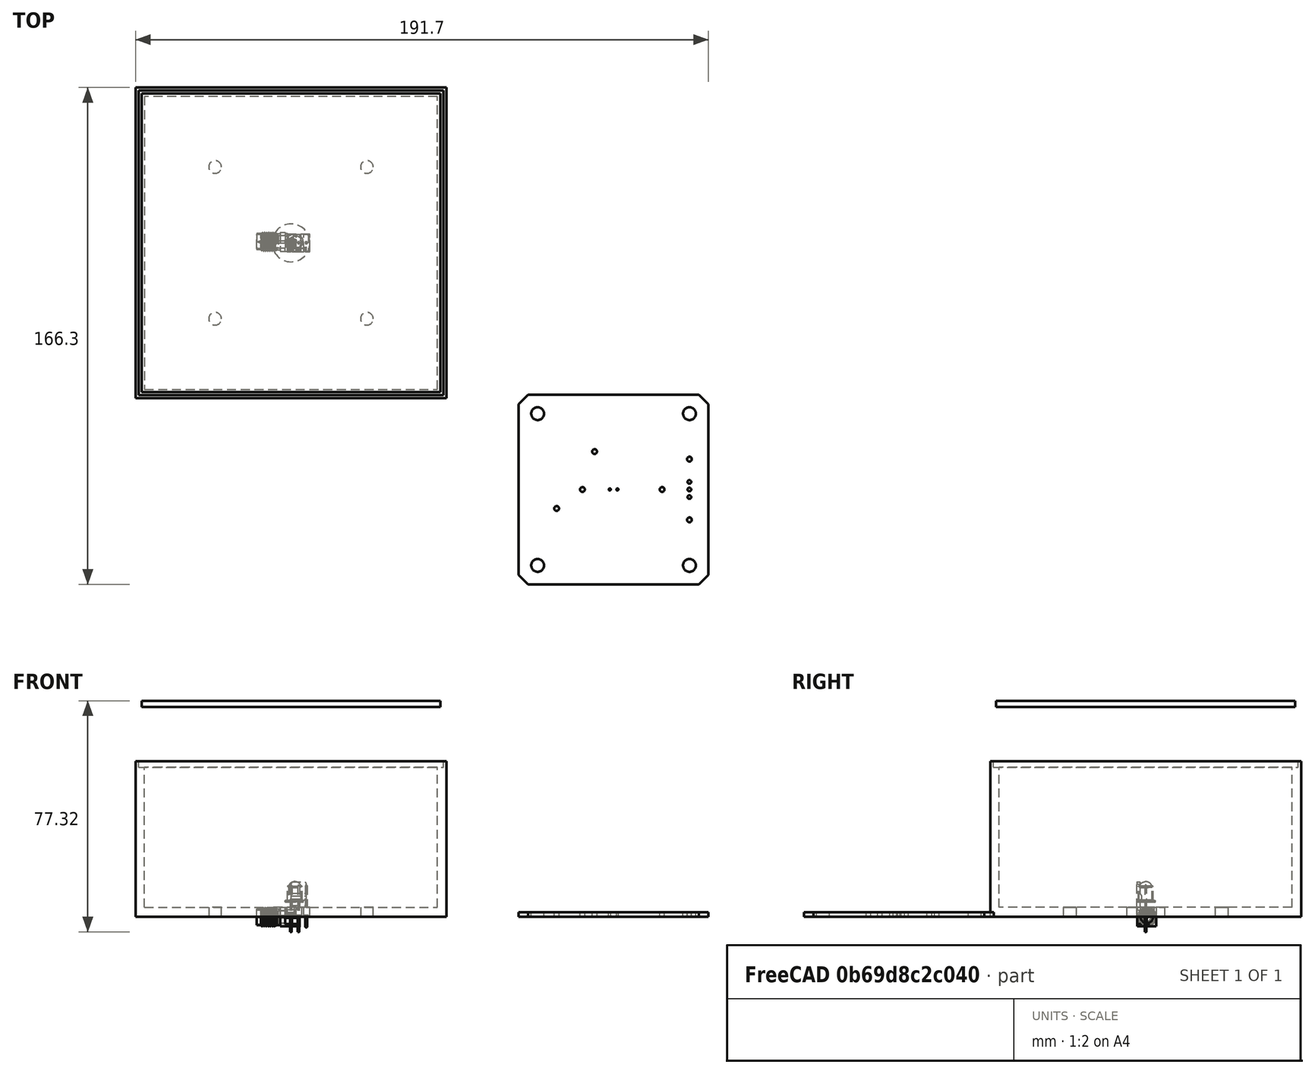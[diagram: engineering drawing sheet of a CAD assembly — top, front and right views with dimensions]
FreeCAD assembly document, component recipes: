
FREECAD ASSEMBLY — COMPONENT RECIPES ("Lensmount")

This assembly document has 3 components, labeled P0..P2 below (a component is one placed body or linked part). 2 of them carry a construction recipe — the FreeCAD feature program that regenerates the part from scratch, quoted from this document or its linked companion documents; the rest are supplied as boundary geometry only. No exploded tour is included for this assembly.
COMPONENT P0 — geometry summary ("ADA4610 Transimpedance Amplifier 1"; no construction recipe available for this part):
  bounding box: 73.0 x 63.5 x 18.9 mm
  tessellated surface: 3,265 triangles
  volume: 51078090254027713934101195006140775365494435911598212671501187176010288595226610358736377589302034432 mm^3 (58298447673324615155903128428619562438456596439960692855769413962441940173557407954676489648078848% of its bounding box)
COMPONENT P1 — recipe-attached ("PCB Mount", modeled in this document).
Construction recipe (the document's own serialized feature program — sketch geometry with constraints, then the solid features built on it; lengths are millimeters unless a unit is written):

FEATURE [Sketcher::SketchObject] Sketch
  FullyConstrained = true
  MapMode = 5
  Support = -> [XY_Plane024]
  sketch-geometry (11):
    g0: LineSegment StartX=-52 StartY=-52 StartZ=0 EndX=52 EndY=-52 EndZ=0
    g1: LineSegment StartX=52 StartY=-52 StartZ=0 EndX=52 EndY=52 EndZ=0
    g2: LineSegment StartX=52 StartY=52 StartZ=0 EndX=-52 EndY=52 EndZ=0
    g3: LineSegment StartX=-52 StartY=52 StartZ=0 EndX=-52 EndY=-52 EndZ=0
    g4: LineSegment StartX=-52 StartY=-52 StartZ=0 EndX=52 EndY=52 EndZ=0
    g5: LineSegment StartX=-52 StartY=52 StartZ=0 EndX=52 EndY=-52 EndZ=0
    g6: Circle CenterX=-25.4 CenterY=25.4 CenterZ=0 NormalX=0 NormalY=0 NormalZ=1 AngleXU=0 Radius=2.125
    g7: Circle CenterX=25.4 CenterY=25.4 CenterZ=0 NormalX=0 NormalY=0 NormalZ=1 AngleXU=0 Radius=2.125
    g8: Circle CenterX=25.4 CenterY=-25.4 CenterZ=0 NormalX=0 NormalY=0 NormalZ=1 AngleXU=0 Radius=2.125
    g9: Circle CenterX=-25.4 CenterY=-25.4 CenterZ=0 NormalX=0 NormalY=0 NormalZ=1 AngleXU=0 Radius=2.125
    g10: Circle CenterX=0 CenterY=0 CenterZ=0 NormalX=0 NormalY=0 NormalZ=1 AngleXU=0 Radius=6.35
  constraints (30):
    c: Horizontal(g0)
    c: Horizontal(g2)
    c: Vertical(g1)
    c: Vertical(g3)
    c: DistanceX(g4,g5) = 104
    c: DistanceY(g4,g5) = 104
    c: PointOnObject(g-1,g5)
    c: PointOnObject(g-1,g4)
    c: PointOnObject(g6,g5)
    c: PointOnObject(g7,g4)
    c: PointOnObject(g8,g5)
    c: PointOnObject(g9,g4)
    c: Equal(g6,g7)
    c: Equal(g6,g8)
    c: Equal(g6,g9)
    c: Radius(g6) = 2.125
    c: Coincident(g10,g-1)
    c: Radius(g10) = 6.35
    c: Coincident(g5,g2)
    c: Coincident(g5,g3)
    c: Coincident(g2,g4)
    c: Coincident(g2,g1)
    c: Coincident(g0,g1)
    c: Coincident(g0,g5)
    c: Coincident(g3,g4)
    c: Coincident(g3,g0)
    c: Distance(g6,g10) = 35.921
    c: Distance(g9,g10) = 35.921
    c: Distance(g8,g10) = 35.921
    c: Distance(g7,g10) = 35.921
FEATURE [PartDesign::Pad] Pad
  Direction = (0,0,1)
  Length = 3.175
  Length2 = 9.906
  Profile = -> Sketch
  ReferenceAxis = -> Sketch [N_Axis]
  Type = 0
FEATURE [Sketcher::SketchObject] Sketch002
  FullyConstrained = true
  MapMode = 5
  Placement = pos=(0,0,3.175) rot=(0,0,1;0rad)
  Support = -> [Pad]
FEATURE [Sketcher::SketchObject] Sketch003
  ExternalGeometry = -> [Pad]
  FullyConstrained = true
  MapMode = 5
  Placement = pos=(0,0,3.175) rot=(0,0,1;0rad)
  Support = -> [Pad]
  sketch-geometry (8):
    g0: LineSegment StartX=-52 StartY=-52 StartZ=0 EndX=52 EndY=-52 EndZ=0
    g1: LineSegment StartX=52 StartY=-52 StartZ=0 EndX=52 EndY=52 EndZ=0
    g2: LineSegment StartX=52 StartY=52 StartZ=0 EndX=-52 EndY=52 EndZ=0
    g3: LineSegment StartX=-52 StartY=52 StartZ=0 EndX=-52 EndY=-52 EndZ=0
    g4: LineSegment StartX=-49 StartY=-49 StartZ=0 EndX=49 EndY=-49 EndZ=0
    g5: LineSegment StartX=49 StartY=-49 StartZ=0 EndX=49 EndY=49 EndZ=0
    g6: LineSegment StartX=49 StartY=49 StartZ=0 EndX=-49 EndY=49 EndZ=0
    g7: LineSegment StartX=-49 StartY=49 StartZ=0 EndX=-49 EndY=-49 EndZ=0
  constraints (22):
    c: Coincident(g0,g1)
    c: Coincident(g1,g2)
    c: Coincident(g2,g3)
    c: Coincident(g3,g0)
    c: Horizontal(g0)
    c: Horizontal(g2)
    c: Vertical(g1)
    c: Vertical(g3)
    c: Coincident(g0,g-6)
    c: Coincident(g1,g-5)
    c: Coincident(g4,g5)
    c: Coincident(g5,g6)
    c: Coincident(g6,g7)
    c: Coincident(g7,g4)
    c: Horizontal(g4)
    c: Horizontal(g6)
    c: Vertical(g5)
    c: Vertical(g7)
    c: DistanceY(g6,g2) = 3
    c: DistanceX(g2,g6) = 3
    c: DistanceY(g0,g4) = 3
    c: DistanceX(g4,g0) = 3
FEATURE [PartDesign::Pad] Pad002  label="Walls"
  BaseFeature = -> Pad
  Direction = (0,0,1)
  Length = 46.863
  Length2 = 9.906
  Profile = -> Sketch003
  ReferenceAxis = -> Sketch003 [N_Axis]
  Type = 0
FEATURE [Sketcher::SketchObject] Sketch004
  ExternalGeometry = -> [Pad002]
  FullyConstrained = true
  MapMode = 5
  Placement = pos=(0,0,50.038) rot=(0,0,1;0rad)
  Support = -> [Pad002]
  sketch-geometry (8):
    g0: LineSegment StartX=-52 StartY=-52 StartZ=0 EndX=52 EndY=-52 EndZ=0
    g1: LineSegment StartX=52 StartY=-52 StartZ=0 EndX=52 EndY=52 EndZ=0
    g2: LineSegment StartX=52 StartY=52 StartZ=0 EndX=-52 EndY=52 EndZ=0
    g3: LineSegment StartX=-52 StartY=52 StartZ=0 EndX=-52 EndY=-52 EndZ=0
    g4: LineSegment StartX=-50.984 StartY=-50.984 StartZ=0 EndX=50.984 EndY=-50.984 EndZ=0
    g5: LineSegment StartX=50.984 StartY=-50.984 StartZ=0 EndX=50.984 EndY=50.984 EndZ=0
    g6: LineSegment StartX=50.984 StartY=50.984 StartZ=0 EndX=-50.984 EndY=50.984 EndZ=0
    g7: LineSegment StartX=-50.984 StartY=50.984 StartZ=0 EndX=-50.984 EndY=-50.984 EndZ=0
  constraints (22):
    c: Coincident(g0,g1)
    c: Coincident(g1,g2)
    c: Coincident(g2,g3)
    c: Coincident(g3,g0)
    c: Horizontal(g0)
    c: Horizontal(g2)
    c: Vertical(g1)
    c: Vertical(g3)
    c: Coincident(g0,g-4)
    c: Coincident(g1,g-3)
    c: Coincident(g4,g5)
    c: Coincident(g5,g6)
    c: Coincident(g6,g7)
    c: Coincident(g7,g4)
    c: Horizontal(g4)
    c: Horizontal(g6)
    c: Vertical(g5)
    c: Vertical(g7)
    c: DistanceX(g2,g6) = 1.016
    c: DistanceY(g6,g2) = 1.016
    c: DistanceY(g0,g4) = 1.016
    c: DistanceX(g4,g0) = 1.016
FEATURE [PartDesign::Pad] Pad003
  BaseFeature = -> Pad002
  Direction = (0,0,1)
  Length = 2
  Length2 = 9.906
  Profile = -> Sketch004
  ReferenceAxis = -> Sketch004 [N_Axis]
  Type = 0
FEATURE [PartDesign::CoordinateSystem] LCS_MH1
  AttacherType = Attacher::AttachEngine3D
  MapMode = 11
  Placement = pos=(-25.4,-25.4,0) rot=(0,0,1;1.5708rad)
  Support = -> [Pad003]
FEATURE [PartDesign::CoordinateSystem] LCS_LENS
  AttacherType = Attacher::AttachEngine3D
  MapMode = 45
  Placement = pos=(-3.21e-14,-6.2e-15,50.038) rot=(0,0,1;0rad)
  Support = -> [Pad003]
FEATURE [PartDesign::Body] Body  label="PCB Mount"
  Group = -> [Sketch,Pad,Sketch002,Sketch003,Pad002,Sketch004,Pad003,LCS_MH1,LCS_LENS]
  Origin = -> Origin024
  Tip = -> Pad003
COMPONENT P2 — recipe-attached ("Lens", modeled in this document).
Construction recipe (the document's own serialized feature program — sketch geometry with constraints, then the solid features built on it; lengths are millimeters unless a unit is written):

FEATURE [Sketcher::SketchObject] Sketch001
  FullyConstrained = true
  MapMode = 5
  Support = -> [XY_Plane025]
  sketch-geometry (6):
    g0: LineSegment StartX=-50 StartY=-50 StartZ=0 EndX=50 EndY=-50 EndZ=0
    g1: LineSegment StartX=50 StartY=-50 StartZ=0 EndX=50 EndY=50 EndZ=0
    g2: LineSegment StartX=50 StartY=50 StartZ=0 EndX=-50 EndY=50 EndZ=0
    g3: LineSegment StartX=-50 StartY=50 StartZ=0 EndX=-50 EndY=-50 EndZ=0
    g4: LineSegment StartX=-50 StartY=-50 StartZ=0 EndX=50 EndY=50 EndZ=0
    g5: LineSegment StartX=50 StartY=-50 StartZ=0 EndX=-50 EndY=50 EndZ=0
  constraints (16):
    c: Coincident(g0,g1)
    c: Coincident(g1,g2)
    c: Coincident(g2,g3)
    c: Coincident(g3,g0)
    c: Horizontal(g0)
    c: Horizontal(g2)
    c: Vertical(g1)
    c: Vertical(g3)
    c: DistanceY(g3,g3) = 100
    c: DistanceX(g0,g0) = 100
    c: Coincident(g4,g0)
    c: Coincident(g4,g1)
    c: Coincident(g5,g0)
    c: Coincident(g5,g2)
    c: PointOnObject(g-1,g5)
    c: PointOnObject(g-1,g4)
FEATURE [PartDesign::Pad] Pad001
  Direction = (0,0,1)
  Length = 2
  Length2 = 9.906
  Profile = -> Sketch001
  ReferenceAxis = -> Sketch001 [N_Axis]
  Type = 0
FEATURE [PartDesign::CoordinateSystem] LCS_1
  AttacherType = Attacher::AttachEngine3D
  MapMode = 45
  Placement = pos=(-2e-16,0,0) rot=(0,0,1;0rad)
  Support = -> [Pad001]
FEATURE [PartDesign::Body] Body001  label="Lens"
  Group = -> [Sketch001,Pad001,LCS_1]
  Origin = -> Origin025
  Placement = pos=(0,0,70.32) rot=(0,0,1;0rad)
  Tip = -> Pad001
PROVENANCE & LICENSES
A FreeCAD (.FCStd) document from a public repository crawl; recipes are the document's own serialized feature recipes (and, for linked parts, companion documents' recipes).
License: gpl-3.0.
